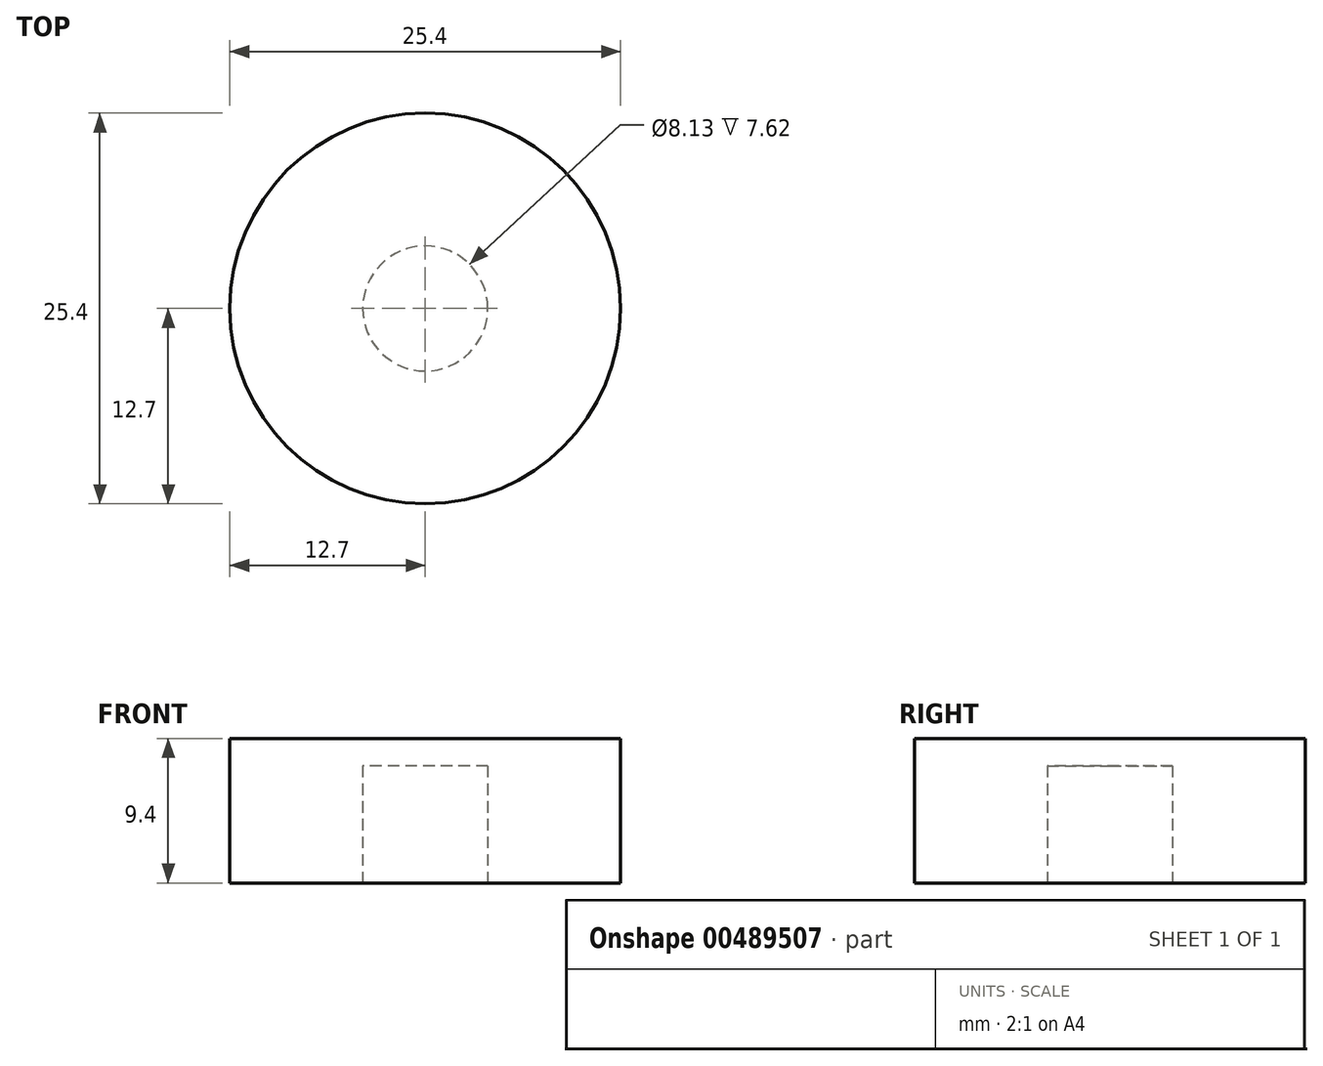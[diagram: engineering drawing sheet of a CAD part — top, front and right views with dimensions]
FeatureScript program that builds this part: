
annotation { "Feature Type Name" : "Feature", "Feature Type Description" : "" }
export const myFeature = defineFeature(function(context is Context, id is Id, definition is map)
    precondition{}
    {
        {
            var Q0;
            Q0=qCreatedBy(makeId("Top.planeOp"),FACE);
            var sketch = newSketch(context, id + "F0", { "sketchPlane" : qUnion([Q0])});
            skCircle(sketch, "E0", {"center": v(0, 0) * mm, "radius": 12.7 * mm});
            skCircle(sketch, "E1", {"center": v(0, 0) * mm, "radius": 4.06 * mm});
            skSolve(sketch);
        }
        {
            var Q0;
            Q0 = qSketchRegion(id + "F0", true);
            extrude(context, id + "F1", {"entities" : qUnion([Q0]), "depth" : 7.62 * mm, "offsetDistance" : 25.4 * mm});
        }
        {
            var Q0;
            Q0=makeQuery(id+"F1.opExtrude","CAP_FACE",FACE,{"disambiguationData":[OSD([sQuery(id+"F0.wireOp",EDGE,"E0"),sQuery(id+"F0.wireOp",EDGE,"E1")])],"isStart":false});
            var sketch = newSketch(context, id + "F2", { "sketchPlane" : qUnion([Q0])});
            skCircle(sketch, "E2", {"center": v(0, 0) * mm, "radius": 12.7 * mm});
            skSolve(sketch);
        }
        {
            var Q0;
            Q0 = qSketchRegion(id + "F2", true);
            extrude(context, id + "F3", {"entities" : qUnion([Q0]), "operationType" : NewBodyOperationType.ADD, "depth" : 1.78 * mm, "offsetDistance" : 25.4 * mm});
        }
    });
